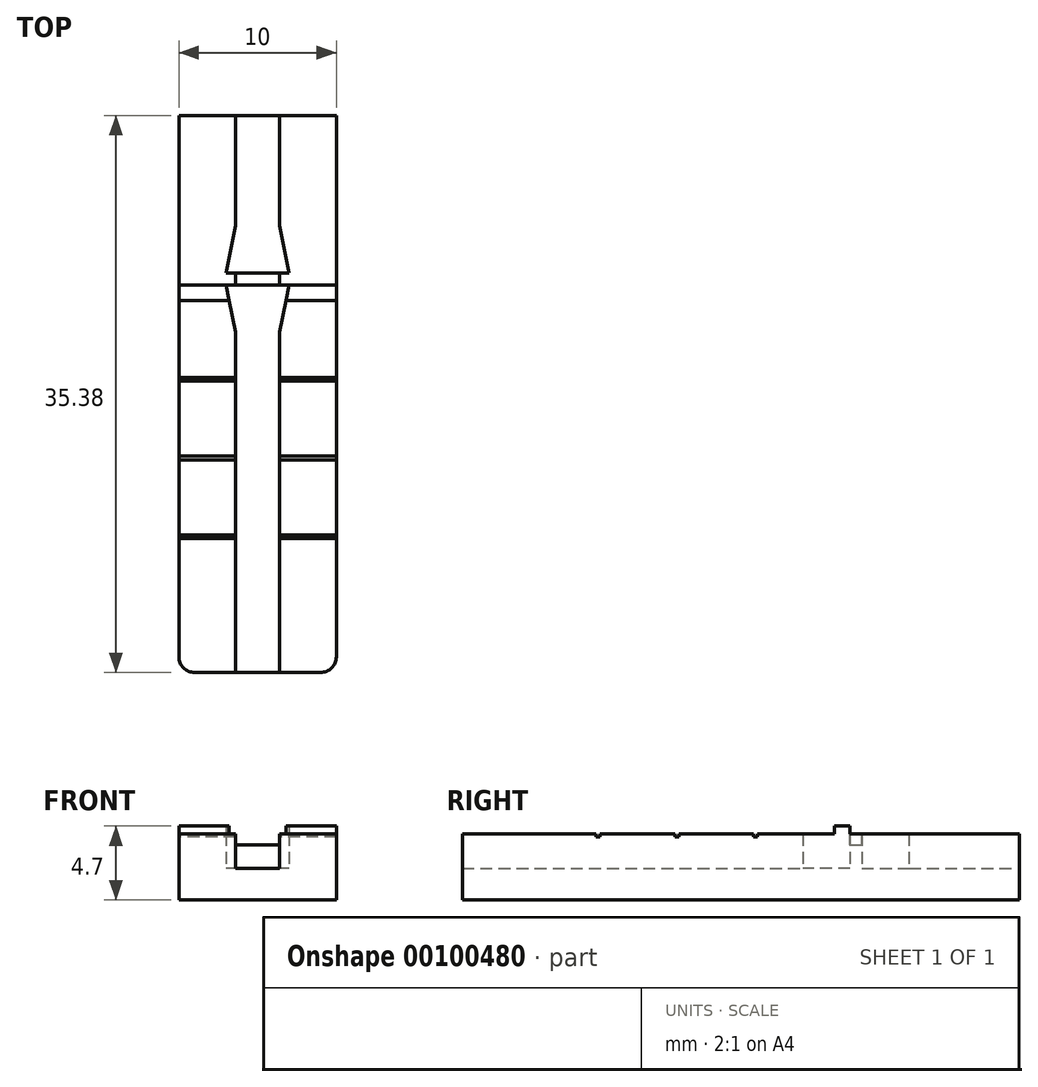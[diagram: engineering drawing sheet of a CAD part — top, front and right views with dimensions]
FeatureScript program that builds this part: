
annotation { "Feature Type Name" : "Feature", "Feature Type Description" : "" }
export const myFeature = defineFeature(function(context is Context, id is Id, definition is map)
    precondition{}
    {
        {
            var Q0;
            Q0=qCreatedBy(makeId("Front.planeOp"),FACE);
            var sketch = newSketch(context, id + "F0", { "sketchPlane" : qUnion([Q0])});
            skLineSegment(sketch, "E0", {"start": v(-5, 0) * mm, "end": v(5, 0) * mm});
            skLineSegment(sketch, "E1", {"start": v(5, 0) * mm, "end": v(5, 4.2) * mm});
            skLineSegment(sketch, "E2", {"start": v(5, 4.2) * mm, "end": v(1.4, 4.2) * mm});
            skLineSegment(sketch, "E3", {"start": v(1.4, 4.2) * mm, "end": v(1.4, 2) * mm});
            skLineSegment(sketch, "E4", {"start": v(1.4, 2) * mm, "end": v(-1.4, 2) * mm});
            skLineSegment(sketch, "E5", {"start": v(-1.4, 2) * mm, "end": v(-1.4, 4.2) * mm});
            skLineSegment(sketch, "E6", {"start": v(-1.4, 4.2) * mm, "end": v(-5, 4.2) * mm});
            skLineSegment(sketch, "E7", {"start": v(-5, 4.2) * mm, "end": v(-5, 0) * mm});
            skPoint(sketch, "E8", {"position": v(0, 2) * mm});
            skSolve(sketch);
        }
        {
            var Q0;
            Q0 = qSketchRegion(id + "F0", true);
            extrude(context, id + "F1", {"entities" : qUnion([Q0]), "endBound" : BoundingType.SYMMETRIC, "depth" : 50 * mm});
        }
        {
            var Q0;
            Q0=makeQuery(id+"F1.opExtrude","SWEPT_FACE",FACE,{"disambiguationData":[OSD([sQuery(id+"F0.wireOp",EDGE,"E4")])]});
            var sketch = newSketch(context, id + "F2", { "sketchPlane" : qUnion([Q0])});
            skLineSegment(sketch, "E9.bottom", {"start": v(1.4, 0.38) * mm, "end": v(-1.4, 0.38) * mm});
            skLineSegment(sketch, "E9.top", {"start": v(1.4, -0.38) * mm, "end": v(-1.4, -0.38) * mm});
            skLineSegment(sketch, "E9.left", {"start": v(1.4, 0.38) * mm, "end": v(1.4, -0.38) * mm});
            skLineSegment(sketch, "E9.right", {"start": v(-1.4, 0.38) * mm, "end": v(-1.4, -0.38) * mm});
            skPoint(sketch, "E9.middle", {"position": v(0, 0) * mm});
            skSolve(sketch);
        }
        {
            var Q0;
            Q0 = qSketchRegion(id + "F2", true);
            extrude(context, id + "F3", {"entities" : qUnion([Q0]), "operationType" : NewBodyOperationType.ADD, "depth" : 1.5 * mm});
        }
        {
            var Q0;
            Q0=makeQuery(id+"F1.opExtrude","SWEPT_FACE",FACE,{"disambiguationData":[OSD([sQuery(id+"F0.wireOp",EDGE,"E6")])]});
            var sketch = newSketch(context, id + "F4", { "sketchPlane" : qUnion([Q0])});
            skLineSegment(sketch, "E10.bottom", {"start": v(5, -0.37) * mm, "end": v(-5, -0.38) * mm});
            skLineSegment(sketch, "E10.top", {"start": v(5, -1.37) * mm, "end": v(-5, -1.38) * mm});
            skLineSegment(sketch, "E10.left", {"start": v(5, -0.38) * mm, "end": v(5, -1.37) * mm});
            skLineSegment(sketch, "E10.right", {"start": v(-5, -0.38) * mm, "end": v(-5, -1.37) * mm});
            skLineSegment(sketch, "E11", {"start": v(-1.4, -0.38) * mm, "end": v(-1.4, -1.37) * mm});
            skLineSegment(sketch, "E12", {"start": v(1.4, -1.37) * mm, "end": v(1.4, -0.38) * mm});
            skSolve(sketch);
        }
        {
            var Q0;
            {var subQ0=sQuery(id+"F4.wireOp",EDGE,"E10.left");Q0=makeQuery(id+"F4.imprint","IMPRINT",FACE,{"disambiguationData":[TD([[makeQuery(id+"F4.imprint","IMPRINT",EDGE,{"derivedFrom":subQ0}),-1.0]])]});}
            var Q1;
            {var subQ0=sQuery(id+"F4.wireOp",EDGE,"E10.right");Q1=makeQuery(id+"F4.imprint","IMPRINT",FACE,{"disambiguationData":[TD([[makeQuery(id+"F4.imprint","IMPRINT",EDGE,{"derivedFrom":subQ0}),-1.0]])]});}
            extrude(context, id + "F5", {"entities" : qUnion([Q0, Q1]), "operationType" : NewBodyOperationType.ADD, "depth" : .5 * mm});
        }
        {
            var Q0;
            {var subQ1=sQuery(id+"F4.wireOp",EDGE,"E10.right");var subQ2=sQuery(id+"F4.wireOp",EDGE,"E10.top");var subQ3=sQuery(id+"F0.wireOp",EDGE,"E7");var subQ4=sQuery(id+"F0.wireOp",EDGE,"E6");Q0=makeQuery(id+"F5.boolean.opBoolean","SPLIT",FACE,{"disambiguationData":[TD([makeQuery(id+"F5.opExtrude","SWEPT_FACE",FACE,{"disambiguationData":[OSD([subQ2]),TDD([makeQuery(id+"F4.imprint","IMPRINT",EDGE,{"disambiguationData":[TD([[makeQuery(id+"F4.imprint","INTERSECT",VERTEX,{"derivedFrom":[makeQuery(id+"F1.opExtrude","SWEPT_EDGE",EDGE,{"disambiguationData":[OSD([subQ4,subQ3])]}),subQ2,subQ1]}),1.0]])],"derivedFrom":subQ2})])]})])],"derivedFrom":makeQuery(id+"F1.opExtrude","SWEPT_FACE",FACE,{"disambiguationData":[OSD([subQ4])]})});}
            var sketch = newSketch(context, id + "F6", { "sketchPlane" : qUnion([Q0])});
            skLineSegment(sketch, "E13.bottom", {"start": v(5, -6.5) * mm, "end": v(-5, -6.5) * mm});
            skLineSegment(sketch, "E13.top", {"start": v(5, -6.25) * mm, "end": v(-5, -6.25) * mm});
            skLineSegment(sketch, "E13.left", {"start": v(5, -6.5) * mm, "end": v(5, -6.25) * mm});
            skLineSegment(sketch, "E13.right", {"start": v(-5, -6.5) * mm, "end": v(-5, -6.25) * mm});
            skPoint(sketch, "E13.middle", {"position": v(0, -6.37) * mm});
            skLineSegment(sketch, "E14.bottom", {"start": v(5, -11.5) * mm, "end": v(-5, -11.5) * mm});
            skLineSegment(sketch, "E14.top", {"start": v(5, -11.25) * mm, "end": v(-5, -11.25) * mm});
            skLineSegment(sketch, "E14.left", {"start": v(5, -11.5) * mm, "end": v(5, -11.25) * mm});
            skLineSegment(sketch, "E14.right", {"start": v(-5, -11.5) * mm, "end": v(-5, -11.25) * mm});
            skPoint(sketch, "E14.middle", {"position": v(0, -11.37) * mm});
            skLineSegment(sketch, "E15.bottom", {"start": v(5, -16.5) * mm, "end": v(-5, -16.5) * mm});
            skLineSegment(sketch, "E15.top", {"start": v(5, -16.25) * mm, "end": v(-5, -16.25) * mm});
            skLineSegment(sketch, "E15.left", {"start": v(5, -16.5) * mm, "end": v(5, -16.25) * mm});
            skLineSegment(sketch, "E15.right", {"start": v(-5, -16.5) * mm, "end": v(-5, -16.25) * mm});
            skPoint(sketch, "E15.middle", {"position": v(0, -16.37) * mm});
            skSolve(sketch);
        }
        {
            var Q0;
            Q0 = qSketchRegion(id + "F6", true);
            extrude(context, id + "F7", {"entities" : qUnion([Q0]), "operationType" : NewBodyOperationType.REMOVE, "oppositeDirection" : true, "depth" : .2 * mm});
        }
        {
            var Q0;
            {var subQ0=sQuery(id+"F4.wireOp",EDGE,"E10.left");var subQ1=sQuery(id+"F4.wireOp",EDGE,"E10.bottom");var subQ5=sQuery(id+"F0.wireOp",EDGE,"E2");Q0=makeQuery(id+"F5.boolean.opBoolean","SPLIT",FACE,{"disambiguationData":[TD([makeQuery(id+"F5.opExtrude","SWEPT_FACE",FACE,{"disambiguationData":[OSD([subQ1]),TDD([makeQuery(id+"F4.imprint","IMPRINT",EDGE,{"disambiguationData":[TD([[makeQuery(id+"F4.imprint","INTERSECT",VERTEX,{"derivedFrom":[subQ1,subQ0]}),-1.0]])],"derivedFrom":subQ1})])]})])],"derivedFrom":makeQuery(id+"F1.opExtrude","SWEPT_FACE",FACE,{"disambiguationData":[OSD([subQ5])]})});}
            var sketch = newSketch(context, id + "F8", { "sketchPlane" : qUnion([Q0])});
            skLineSegment(sketch, "E16.bottom", {"start": v(5, 25) * mm, "end": v(-5, 25) * mm});
            skLineSegment(sketch, "E16.top", {"start": v(5, 10.38) * mm, "end": v(-5, 10.38) * mm});
            skLineSegment(sketch, "E16.left", {"start": v(5, 25) * mm, "end": v(5, 10.38) * mm});
            skLineSegment(sketch, "E16.right", {"start": v(-5, 25) * mm, "end": v(-5, 10.38) * mm});
            skSolve(sketch);
        }
        {
            var Q0;
            Q0 = qSketchRegion(id + "F8", true);
            extrude(context, id + "F9", {"entities" : qUnion([Q0]), "operationType" : NewBodyOperationType.REMOVE, "endBound" : BoundingType.THROUGH_ALL, "oppositeDirection" : true, "depth" : 25 * mm});
        }
        {
            var Q0;
            Q0=makeQuery(id+"F9.boolean.opBoolean","COPY",EDGE,{"derivedFrom":makeQuery(id+"F9.opExtrude","SWEPT_EDGE",EDGE,{"disambiguationData":[OSD([sQuery(id+"F8.wireOp",EDGE,"E16.top"),sQuery(id+"F8.wireOp",EDGE,"E16.right")])]})});
            var Q1;
            Q1=makeQuery(id+"F9.boolean.opBoolean","COPY",EDGE,{"derivedFrom":makeQuery(id+"F9.opExtrude","SWEPT_EDGE",EDGE,{"disambiguationData":[OSD([sQuery(id+"F0.wireOp",EDGE,"E1"),sQuery(id+"F0.wireOp",EDGE,"E2"),sQuery(id+"F8.wireOp",EDGE,"E16.top"),sQuery(id+"F8.wireOp",EDGE,"E16.left")])]})});
            var Q2;
            Q2=makeQuery(id+"F1.opExtrude","CAP_EDGE",EDGE,{"disambiguationData":[OSD([sQuery(id+"F0.wireOp",EDGE,"E7")])],"isStart":false});
            var Q3;
            Q3=makeQuery(id+"F1.opExtrude","CAP_EDGE",EDGE,{"disambiguationData":[OSD([sQuery(id+"F0.wireOp",EDGE,"E1")])],"isStart":false});
            fillet(context, id + "F10", {"entities" : qUnion([Q0, Q1, Q2, Q3]), "radius" : 1 * mm, "tangentPropagation" : true, "allowEdgeOverflow" : false});
        }
        {
            var Q0;
            {var subQ1=sQuery(id+"F0.wireOp",EDGE,"E4");Q0=makeQuery(id+"F3.boolean.opBoolean","SPLIT",FACE,{"disambiguationData":[TD([makeQuery(id+"F3.opExtrude","SWEPT_FACE",FACE,{"disambiguationData":[OSD([sQuery(id+"F2.wireOp",EDGE,"E9.top")])]})])],"derivedFrom":makeQuery(id+"F1.opExtrude","SWEPT_FACE",FACE,{"disambiguationData":[OSD([subQ1])]})});}
            var sketch = newSketch(context, id + "F11", { "sketchPlane" : qUnion([Q0])});
            skLineSegment(sketch, "E17", {"start": v(-2, -0.38) * mm, "end": v(2, -0.38) * mm});
            skLineSegment(sketch, "E18", {"start": v(2, -0.37) * mm, "end": v(1.4, -3.38) * mm});
            skLineSegment(sketch, "E19", {"start": v(-1.4, -3.38) * mm, "end": v(-2, -0.37) * mm});
            skLineSegment(sketch, "E20", {"start": v(1.4, -3.38) * mm, "end": v(-1.4, -3.38) * mm});
            skLineSegment(sketch, "E21", {"start": v(-1.4, 0) * mm, "end": v(1.4, 0) * mm, "construction": true});
            skLineSegment(sketch, "E22.MirrorCS", {"start": v(-2, 0.38) * mm, "end": v(2, 0.38) * mm});
            skLineSegment(sketch, "E23.MirrorCS", {"start": v(1.4, 3.38) * mm, "end": v(-1.4, 3.38) * mm});
            skLineSegment(sketch, "E24.MirrorCS", {"start": v(-1.4, 3.38) * mm, "end": v(-2, 0.37) * mm});
            skLineSegment(sketch, "E25.MirrorCS", {"start": v(2, 0.37) * mm, "end": v(1.4, 3.38) * mm});
            skSolve(sketch);
        }
        {
            var Q0;
            Q0 = qSketchRegion(id + "F11", true);
            extrude(context, id + "F12", {"entities" : qUnion([Q0]), "operationType" : NewBodyOperationType.REMOVE, "endBound" : BoundingType.THROUGH_ALL, "depth" : 25 * mm});
        }
    });
